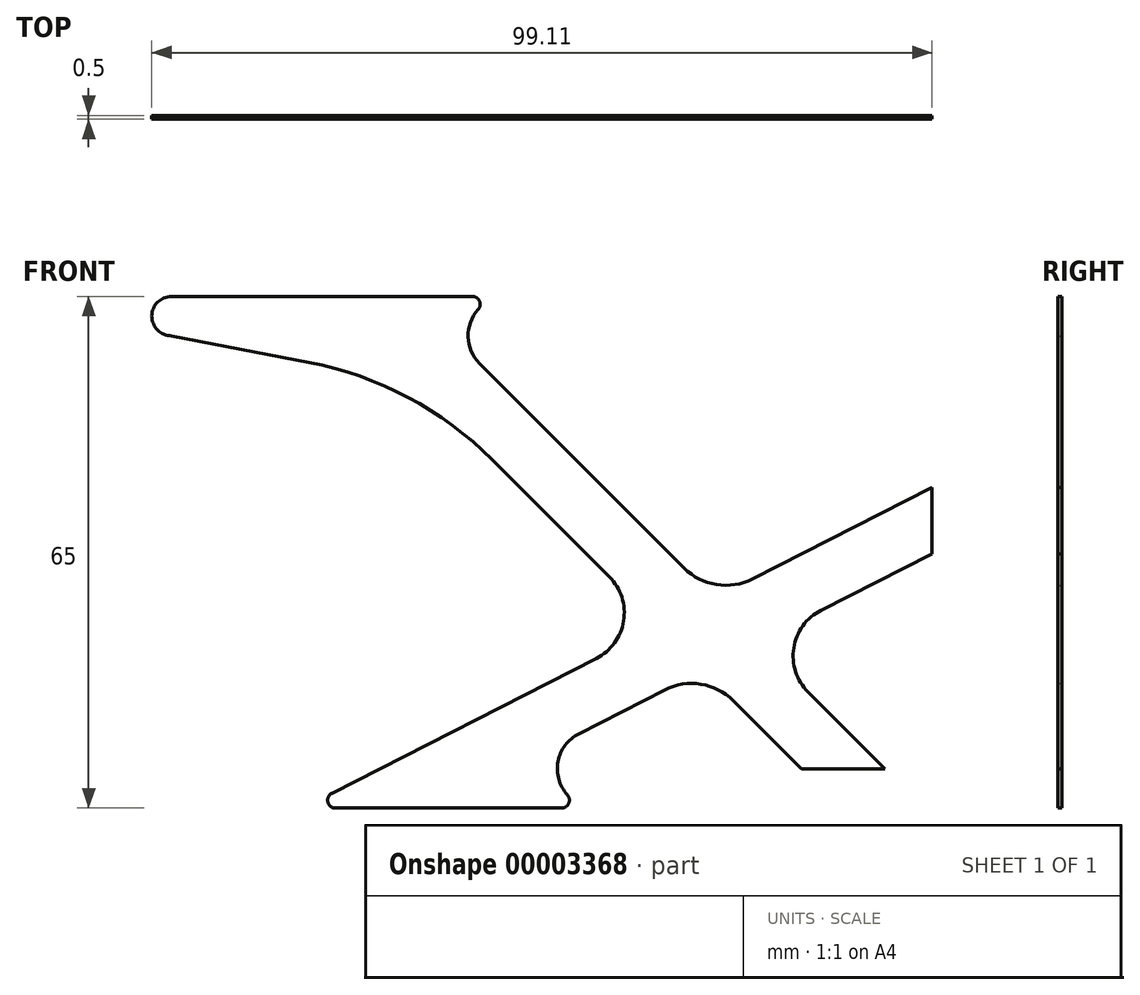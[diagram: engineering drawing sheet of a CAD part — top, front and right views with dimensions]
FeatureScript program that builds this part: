
annotation { "Feature Type Name" : "Feature", "Feature Type Description" : "" }
export const myFeature = defineFeature(function(context is Context, id is Id, definition is map)
    precondition{}
    {
        {
            var Q0;
            Q0=qCreatedBy(makeId("Front.planeOp"),FACE);
            var sketch = newSketch(context, id + "F0", { "sketchPlane" : qUnion([Q0])});
            skLineSegment(sketch, "E0", {"start": v(10.6, 0) * mm, "end": v(0.86, 9.74) * mm});
            skLineSegment(sketch, "E1", {"start": v(0, 0) * mm, "end": v(-8.64, 8.64) * mm});
            skLineSegment(sketch, "E2", {"start": v(16.6, 35.73) * mm, "end": v(-6.18, 24.12) * mm});
            skLineSegment(sketch, "E3", {"start": v(-28.26, 4.46) * mm, "end": v(-17.34, 10.02) * mm});
            skLineSegment(sketch, "E4", {"start": v(10.6, 0) * mm, "end": v(0, 0) * mm});
            skLineSegment(sketch, "E5.trimOffspring", {"start": v(-24.4, 24.4) * mm, "end": v(-39.26, 39.26) * mm});
            skPoint(sketch, "E6.visualSharp", {"position": v(-18.07, 18.07) * mm});
            skArc(sketch, "E6.filletArc", {"start": v(-26.04, 14) * mm, "mid": v(-22.57, 18.78) * mm, "end": v(-24.4, 24.4) * mm});
            skPoint(sketch, "E7.visualSharp", {"position": v(-12.49, 12.49) * mm});
            skArc(sketch, "E7.filletArc", {"start": v(-8.64, 8.64) * mm, "mid": v(-12.77, 10.74) * mm, "end": v(-17.34, 10.02) * mm});
            skLineSegment(sketch, "E8", {"start": v(-80, 55) * mm, "end": v(-62.53, 51.62) * mm});
            skPoint(sketch, "E9.visualSharp", {"position": v(-49, 49) * mm});
            skArc(sketch, "E9.filletArc", {"start": v(-39.26, 39.26) * mm, "mid": v(-49.97, 47.18) * mm, "end": v(-62.53, 51.62) * mm});
            skLineSegment(sketch, "E10", {"start": v(16.6, 27.31) * mm, "end": v(16.6, 35.73) * mm});
            skLineSegment(sketch, "E11.trimOffspring", {"start": v(-14.9, 25.5) * mm, "end": v(-40.86, 51.46) * mm});
            skLineSegment(sketch, "E12.trimOffspring", {"start": v(-26.04, 14) * mm, "end": v(-59.62, -3.1) * mm});
            skLineSegment(sketch, "E13.trimOffspring", {"start": v(2.5, 20.13) * mm, "end": v(16.6, 27.31) * mm});
            skPoint(sketch, "E14.visualSharp", {"position": v(-11.04, 21.65) * mm});
            skArc(sketch, "E14.filletArc", {"start": v(-14.9, 25.5) * mm, "mid": v(-10.76, 23.4) * mm, "end": v(-6.18, 24.12) * mm});
            skPoint(sketch, "E15.visualSharp", {"position": v(-5.46, 16.07) * mm});
            skArc(sketch, "E15.filletArc", {"start": v(2.5, 20.13) * mm, "mid": v(-0.96, 15.36) * mm, "end": v(0.86, 9.74) * mm});
            skArc(sketch, "E16.filletArc", {"start": v(-28.26, 4.46) * mm, "mid": v(-30.9, 0.92) * mm, "end": v(-29.71, -3.33) * mm});
            skLineSegment(sketch, "E17", {"start": v(-59.17, -5) * mm, "end": v(-30.46, -5) * mm});
            skLineSegment(sketch, "E18.0", {"start": v(-41.8, 60) * mm, "end": v(-80, 60) * mm});
            skArc(sketch, "E19.filletArc", {"start": v(-41.05, 58.33) * mm, "mid": v(-42.32, 54.86) * mm, "end": v(-40.86, 51.46) * mm});
            skPoint(sketch, "E20.visualSharp", {"position": v(-37.32, 60) * mm});
            skArc(sketch, "E20.filletArc", {"start": v(-41.05, 58.33) * mm, "mid": v(-40.88, 59.4) * mm, "end": v(-41.8, 60) * mm});
            skPoint(sketch, "E21.visualSharp", {"position": v(-25.99, -5) * mm});
            skArc(sketch, "E21.filletArc", {"start": v(-30.46, -5) * mm, "mid": v(-29.55, -4.4) * mm, "end": v(-29.71, -3.33) * mm});
            skPoint(sketch, "E22.visualSharp", {"position": v(-63.33, -5) * mm});
            skArc(sketch, "E22.filletArc", {"start": v(-59.62, -3.1) * mm, "mid": v(-60.14, -4.23) * mm, "end": v(-59.17, -5) * mm});
            skArc(sketch, "E23", {"start": v(-80, 55) * mm, "mid": v(-82.5, 57.5) * mm, "end": v(-80, 60) * mm});
            skPoint(sketch, "E24.start.orphan", {"position": v(0, 10.6) * mm});
            skSolve(sketch);
        }
        {
            var Q0;
            Q0=makeQuery(id+"F0.imprint","IMPRINT",FACE,{"disambiguationData":[TD([[makeQuery(id+"F0.imprint","IMPRINT",EDGE,{"derivedFrom":sQuery(id+"F0.wireOp",EDGE,"E0")}),1.0]])]});
            extrude(context, id + "F1", {"entities" : qUnion([Q0]), "depth" : .5 * mm});
        }
    });
